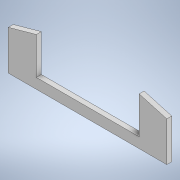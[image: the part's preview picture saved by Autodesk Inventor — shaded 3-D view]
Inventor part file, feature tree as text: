
AUTODESK INVENTOR PART (.ipt)
format: ipt  version: 2020.1 (Build 241239000, 239)  size: 111,616 bytes
history: native  units: in
note: dims shown in document units (in); Inventor stores cm internally (conversion verified against a paired STEP export)
features: extrude x1, sketch x1
ambient origin geometry x8: Origin, YZ Plane, XZ Plane, XY Plane, X Axis, Y Axis, Z Axis, Center Point
bodies: Solid1 (feature_tree)
feature tree (2):
  extrude  "Extrusion1"  Depth=249.0in
  sketch  "Sketch1"  dims[d0=192.0in d1=96.0in d3=68.0in d4=25.0in d5=115.0in d6=192.0in d7=96.0in d8=115.0in d9=12.0in d10=0.0in d11=384.0in d12=67.0in d13=90.0in d14=90.0in d15=70.6045in d16=69.6419in d17=249.0in d18=124.0in d19=125.0in]
